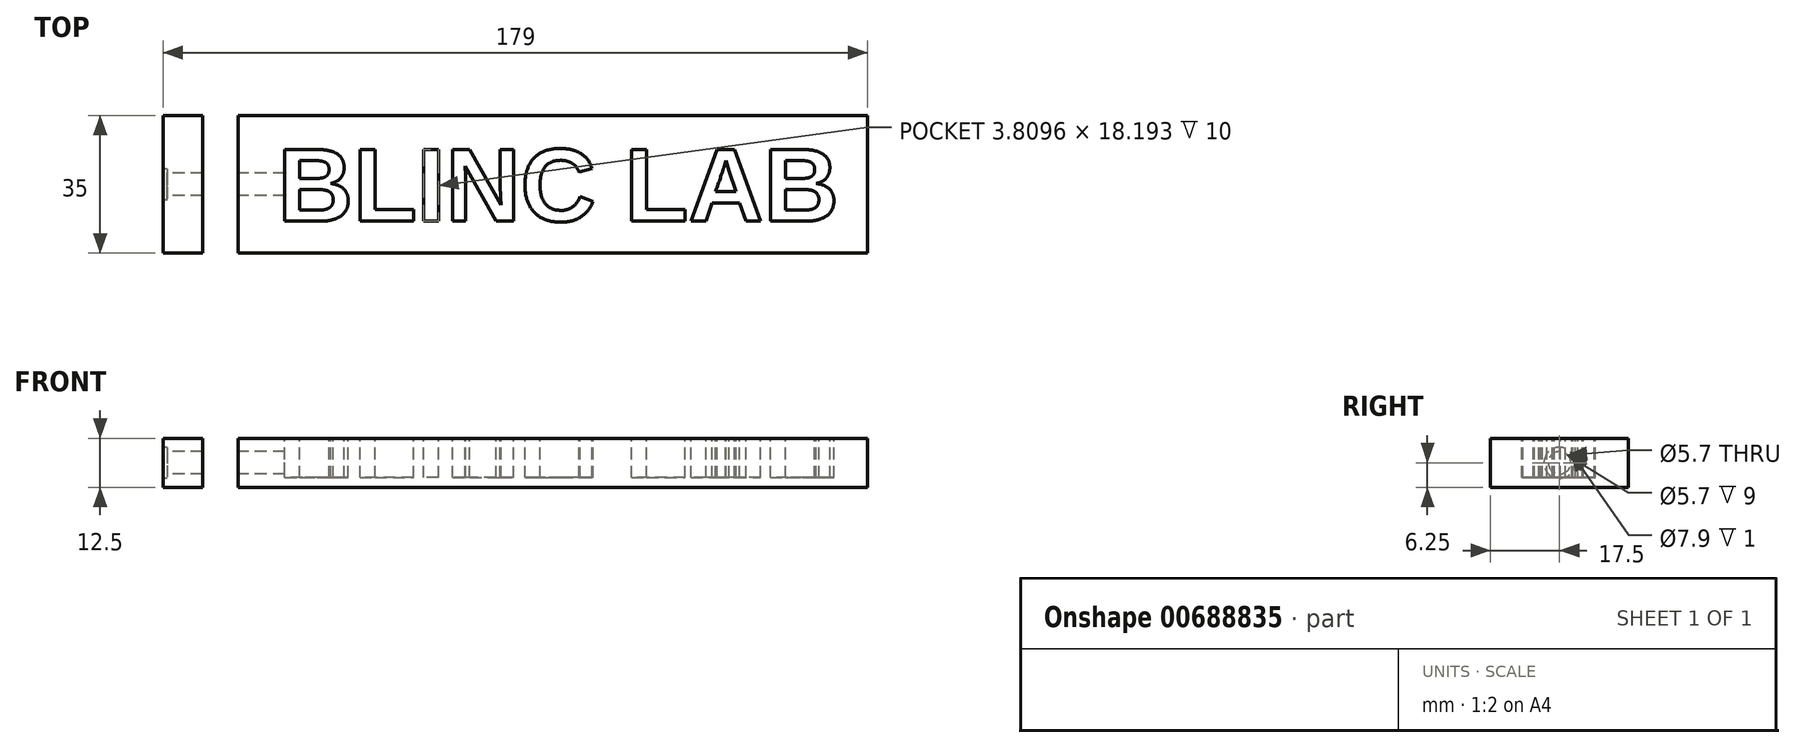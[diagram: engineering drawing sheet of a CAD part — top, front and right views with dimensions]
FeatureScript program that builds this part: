
annotation { "Feature Type Name" : "Feature", "Feature Type Description" : "" }
export const myFeature = defineFeature(function(context is Context, id is Id, definition is map)
    precondition{}
    {
        {
            var Q0;
            Q0=qCreatedBy(makeId("Top.planeOp"),FACE);
            var sketch = newSketch(context, id + "F0", { "sketchPlane" : qUnion([Q0])});
            skLineSegment(sketch, "E0.bottom", {"start": v(80, -17.5) * mm, "end": v(-80, -17.5) * mm});
            skLineSegment(sketch, "E0.top", {"start": v(80, 17.5) * mm, "end": v(-80, 17.5) * mm});
            skLineSegment(sketch, "E0.left", {"start": v(80, -17.5) * mm, "end": v(80, 17.5) * mm});
            skLineSegment(sketch, "E0.right", {"start": v(-80, -17.5) * mm, "end": v(-80, 17.5) * mm});
            skPoint(sketch, "E0.middle", {"position": v(0, 0) * mm});
            skLineSegment(sketch, "E1.left", {"start": v(-89, -6.25) * mm, "end": v(-89, 6.25) * mm});
            skPoint(sketch, "E1.middle", {"position": v(-80, 0) * mm});
            skLineSegment(sketch, "E2.bottom", {"start": v(-89, -17.5) * mm, "end": v(-99, -17.5) * mm});
            skLineSegment(sketch, "E2.top", {"start": v(-89, 17.5) * mm, "end": v(-99, 17.5) * mm});
            skLineSegment(sketch, "E2.left", {"start": v(-89, -17.5) * mm, "end": v(-89, 17.5) * mm});
            skLineSegment(sketch, "E2.right", {"start": v(-99, -17.5) * mm, "end": v(-99, 17.5) * mm});
            skSolve(sketch);
        }
        {
            var Q0;
            Q0 = qSketchRegion(id + "F0", true);
            extrude(context, id + "F1", {"entities" : qUnion([Q0]), "depth" : 12.5 * mm, "offsetDistance" : 25 * mm});
        }
        {
            var Q0;
            Q0=makeQuery(id+"F1.opExtrude","CAP_FACE",FACE,{"disambiguationData":[OSD([sQuery(id+"F0.wireOp",EDGE,"E0.bottom"),sQuery(id+"F0.wireOp",EDGE,"E0.top"),sQuery(id+"F0.wireOp",EDGE,"E0.left"),sQuery(id+"F0.wireOp",EDGE,"E0.right"),sQuery(id+"F0.wireOp",EDGE,"E1.bottom"),sQuery(id+"F0.wireOp",EDGE,"E1.top"),sQuery(id+"F0.wireOp",EDGE,"E2.bottom"),sQuery(id+"F0.wireOp",EDGE,"E2.top"),sQuery(id+"F0.wireOp",EDGE,"E2.left"),sQuery(id+"F0.wireOp",EDGE,"E2.right")])],"isStart":false});
            var sketch = newSketch(context, id + "F2", { "sketchPlane" : qUnion([Q0])});
            skPoint(sketch, "E3.middle", {"position": v(0, 0) * mm});
            skText(sketch, "E4", { "text": "BLINC LAB", "fontName": "Arimo-Bold.ttf"});
            const initialGuessF2  = {"E4": [-0.06987, -0.00935, 1, 0, 0.01904]};
            skSetInitialGuess(sketch, initialGuessF2);
            skSolve(sketch);
        }
        {
            var Q0;
            Q0 = qSketchRegion(id + "F2", true);
            extrude(context, id + "F3", {"entities" : qUnion([Q0]), "operationType" : NewBodyOperationType.REMOVE, "oppositeDirection" : true, "depth" : 10 * mm, "offsetDistance" : 25 * mm});
        }
        {
            var Q0;
            Q0=makeQuery(id+"F1.opExtrude","SWEPT_FACE",FACE,{"disambiguationData":[OSD([sQuery(id+"F0.wireOp",EDGE,"E0.right")])]});
            var sketch = newSketch(context, id + "F4", { "sketchPlane" : qUnion([Q0])});
            skCircle(sketch, "E5", {"center": v(0, 6.25) * mm, "radius": 2.85 * mm});
            skPoint(sketch, "E5.centerSnap0", {"position": v(17.5, 6.25) * mm});
            skSolve(sketch);
        }
        {
            var Q0;
            Q0=makeQuery(id+"F1.opExtrude","SWEPT_FACE",FACE,{"disambiguationData":[OSD([sQuery(id+"F0.wireOp",EDGE,"E2.right")])]});
            var sketch = newSketch(context, id + "F5", { "sketchPlane" : qUnion([Q0])});
            skCircle(sketch, "E6", {"center": v(0, 6.25) * mm, "radius": 2.85 * mm});
            skPoint(sketch, "E6.centerSnap0", {"position": v(17.5, 6.25) * mm});
            skSolve(sketch);
        }
        {
            var Q0;
            Q0=makeQuery(id+"F5.imprint","IMPRINT",FACE,{"disambiguationData":[TD([[makeQuery(id+"F5.imprint","IMPRINT",EDGE,{"derivedFrom":sQuery(id+"F5.wireOp",EDGE,"E6")}),1.0]])]});
            extrude(context, id + "F6", {"entities" : qUnion([Q0]), "operationType" : NewBodyOperationType.REMOVE, "oppositeDirection" : true, "depth" : 25 * mm, "offsetDistance" : 25 * mm});
        }
        {
            var Q0;
            Q0=makeQuery(id+"F4.imprint","IMPRINT",FACE,{"disambiguationData":[TD([[makeQuery(id+"F4.imprint","IMPRINT",EDGE,{"derivedFrom":sQuery(id+"F4.wireOp",EDGE,"E5")}),1.0]])]});
            extrude(context, id + "F7", {"entities" : qUnion([Q0]), "operationType" : NewBodyOperationType.REMOVE, "oppositeDirection" : true, "depth" : 15 * mm, "offsetDistance" : 25 * mm});
        }
        {
            var Q0;
            Q0=makeQuery(id+"F1.opExtrude","SWEPT_FACE",FACE,{"disambiguationData":[OSD([sQuery(id+"F0.wireOp",EDGE,"E2.right")])]});
            var sketch = newSketch(context, id + "F8", { "sketchPlane" : qUnion([Q0])});
            skCircle(sketch, "E7", {"center": v(0, 6.25) * mm, "radius": 3.95 * mm});
            skSolve(sketch);
        }
        {
            var Q0;
            Q0=makeQuery(id+"F8.imprint","IMPRINT",FACE,{"disambiguationData":[TD([[makeQuery(id+"F8.imprint","IMPRINT",EDGE,{"derivedFrom":sQuery(id+"F8.wireOp",EDGE,"E7")}),1.0]])]});
            extrude(context, id + "F9", {"entities" : qUnion([Q0]), "operationType" : NewBodyOperationType.REMOVE, "oppositeDirection" : true, "depth" : 1 * mm, "offsetDistance" : 25 * mm});
        }
    });
